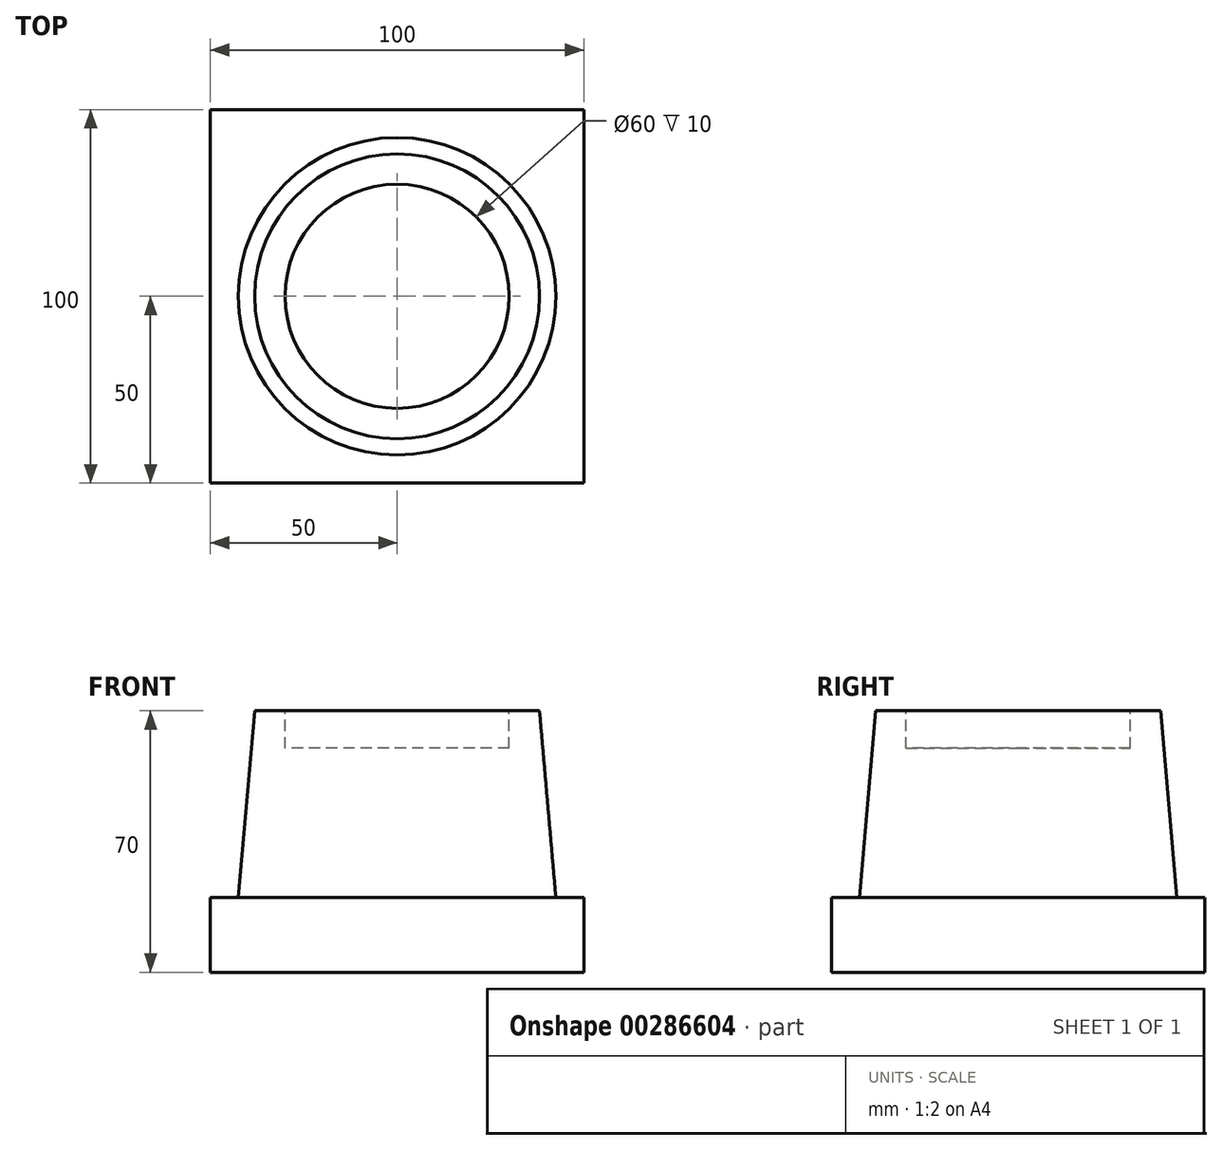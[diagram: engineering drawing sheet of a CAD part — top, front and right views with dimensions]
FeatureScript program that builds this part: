
annotation { "Feature Type Name" : "Feature", "Feature Type Description" : "" }
export const myFeature = defineFeature(function(context is Context, id is Id, definition is map)
    precondition{}
    {
        {
            var Q0;
            Q0=qCreatedBy(makeId("Top.planeOp"),FACE);
            var sketch = newSketch(context, id + "F0", { "sketchPlane" : qUnion([Q0])});
            skLineSegment(sketch, "E0.bottom", {"start": v(-50, 50) * mm, "end": v(50, 50) * mm});
            skLineSegment(sketch, "E0.top", {"start": v(-50, -50) * mm, "end": v(50, -50) * mm});
            skLineSegment(sketch, "E0.left", {"start": v(-50, 50) * mm, "end": v(-50, -50) * mm});
            skLineSegment(sketch, "E0.right", {"start": v(50, 50) * mm, "end": v(50, -50) * mm});
            skPoint(sketch, "E0.middle", {"position": v(0, 0) * mm});
            skSolve(sketch);
        }
        {
            var Q0;
            Q0=makeQuery(id+"F0.imprint","IMPRINT",FACE,{"disambiguationData":[TD([[makeQuery(id+"F0.imprint","IMPRINT",EDGE,{"derivedFrom":sQuery(id+"F0.wireOp",EDGE,"E0.bottom")}),-1.0]])]});
            extrude(context, id + "F1", {"entities" : qUnion([Q0]), "depth" : 20 * mm});
        }
        {
            var Q0;
            Q0=makeQuery(id+"F1.opExtrude","CAP_FACE",FACE,{"disambiguationData":[OSD([sQuery(id+"F0.wireOp",EDGE,"E0.bottom"),sQuery(id+"F0.wireOp",EDGE,"E0.top"),sQuery(id+"F0.wireOp",EDGE,"E0.left"),sQuery(id+"F0.wireOp",EDGE,"E0.right")])],"isStart":false});
            var sketch = newSketch(context, id + "F2", { "sketchPlane" : qUnion([Q0])});
            skCircle(sketch, "E1", {"center": v(0, 0) * mm, "radius": 42.5 * mm});
            skSolve(sketch);
        }
        {
            var Q0;
            Q0=makeQuery(id+"F2.imprint","IMPRINT",FACE,{"disambiguationData":[TD([[makeQuery(id+"F2.imprint","IMPRINT",EDGE,{"derivedFrom":sQuery(id+"F2.wireOp",EDGE,"E1")}),1.0]])]});
            extrude(context, id + "F3", {"entities" : qUnion([Q0]), "operationType" : NewBodyOperationType.ADD, "depth" : 50 * mm, "hasDraft" : true, "draftAngle" : 5 * degree, "draftPullDirection" : true});
        }
        {
            var Q0;
            Q0=makeQuery(id+"F3.opExtrude","CAP_FACE",FACE,{"disambiguationData":[OSD([sQuery(id+"F2.wireOp",EDGE,"E1")])],"isStart":false});
            var sketch = newSketch(context, id + "F4", { "sketchPlane" : qUnion([Q0])});
            skCircle(sketch, "E2", {"center": v(0, 0) * mm, "radius": 30 * mm});
            skSolve(sketch);
        }
        {
            var Q0;
            Q0=makeQuery(id+"F4.imprint","IMPRINT",FACE,{"disambiguationData":[TD([[makeQuery(id+"F4.imprint","IMPRINT",EDGE,{"derivedFrom":sQuery(id+"F4.wireOp",EDGE,"E2")}),1.0]])]});
            extrude(context, id + "F5", {"entities" : qUnion([Q0]), "operationType" : NewBodyOperationType.REMOVE, "oppositeDirection" : true, "depth" : 10 * mm});
        }
    });
